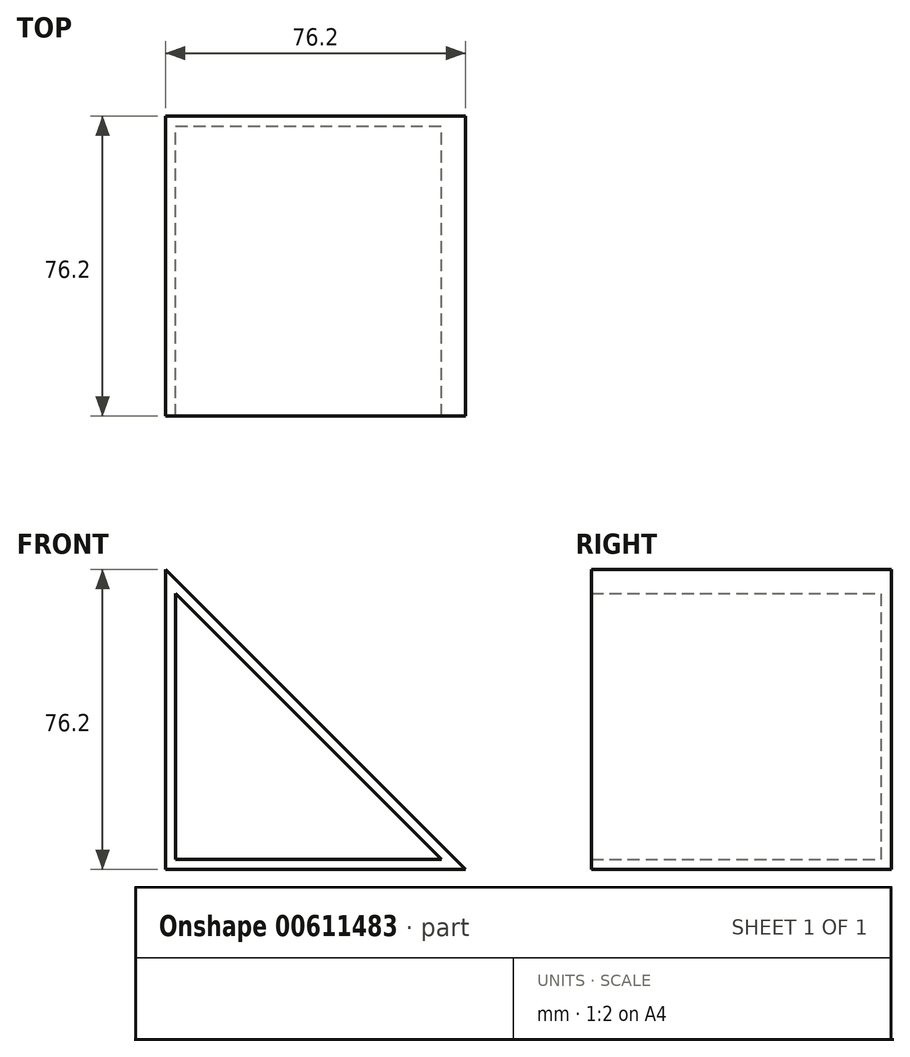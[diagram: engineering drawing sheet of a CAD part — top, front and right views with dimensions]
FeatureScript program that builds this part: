
annotation { "Feature Type Name" : "Feature", "Feature Type Description" : "" }
export const myFeature = defineFeature(function(context is Context, id is Id, definition is map)
    precondition{}
    {
        {
            var Q0;
            Q0=qCreatedBy(makeId("Front.planeOp"),FACE);
            var sketch = newSketch(context, id + "F0", { "sketchPlane" : qUnion([Q0])});
            skLineSegment(sketch, "E0", {"start": v(-76.51, -76.19) * mm, "end": v(-76.51, 0.01) * mm});
            skLineSegment(sketch, "E1", {"start": v(-76.51, -76.19) * mm, "end": v(-0.31, -76.19) * mm});
            skLineSegment(sketch, "E2", {"start": v(-0.31, -76.19) * mm, "end": v(-76.51, 0.01) * mm});
            skSolve(sketch);
        }
        {
            var Q0;
            Q0=makeQuery(id+"F0.imprint","IMPRINT",FACE,{"disambiguationData":[TD([[makeQuery(id+"F0.imprint","IMPRINT",EDGE,{"derivedFrom":sQuery(id+"F0.wireOp",EDGE,"E0")}),-1.0]])]});
            extrude(context, id + "F1", {"entities" : qUnion([Q0]), "depth" : 76.2 * mm, "offsetDistance" : 25.4 * mm});
        }
        {
            var Q0;
            Q0=makeQuery(id+"F1.opExtrude","CAP_FACE",FACE,{"disambiguationData":[OSD([sQuery(id+"F0.wireOp",EDGE,"E0"),sQuery(id+"F0.wireOp",EDGE,"E1"),sQuery(id+"F0.wireOp",EDGE,"E2")])],"isStart":false});
            shell(context, id + "F2", {"entities" : qUnion([Q0]), "thickness" : 2.54 * mm});
        }
    });
